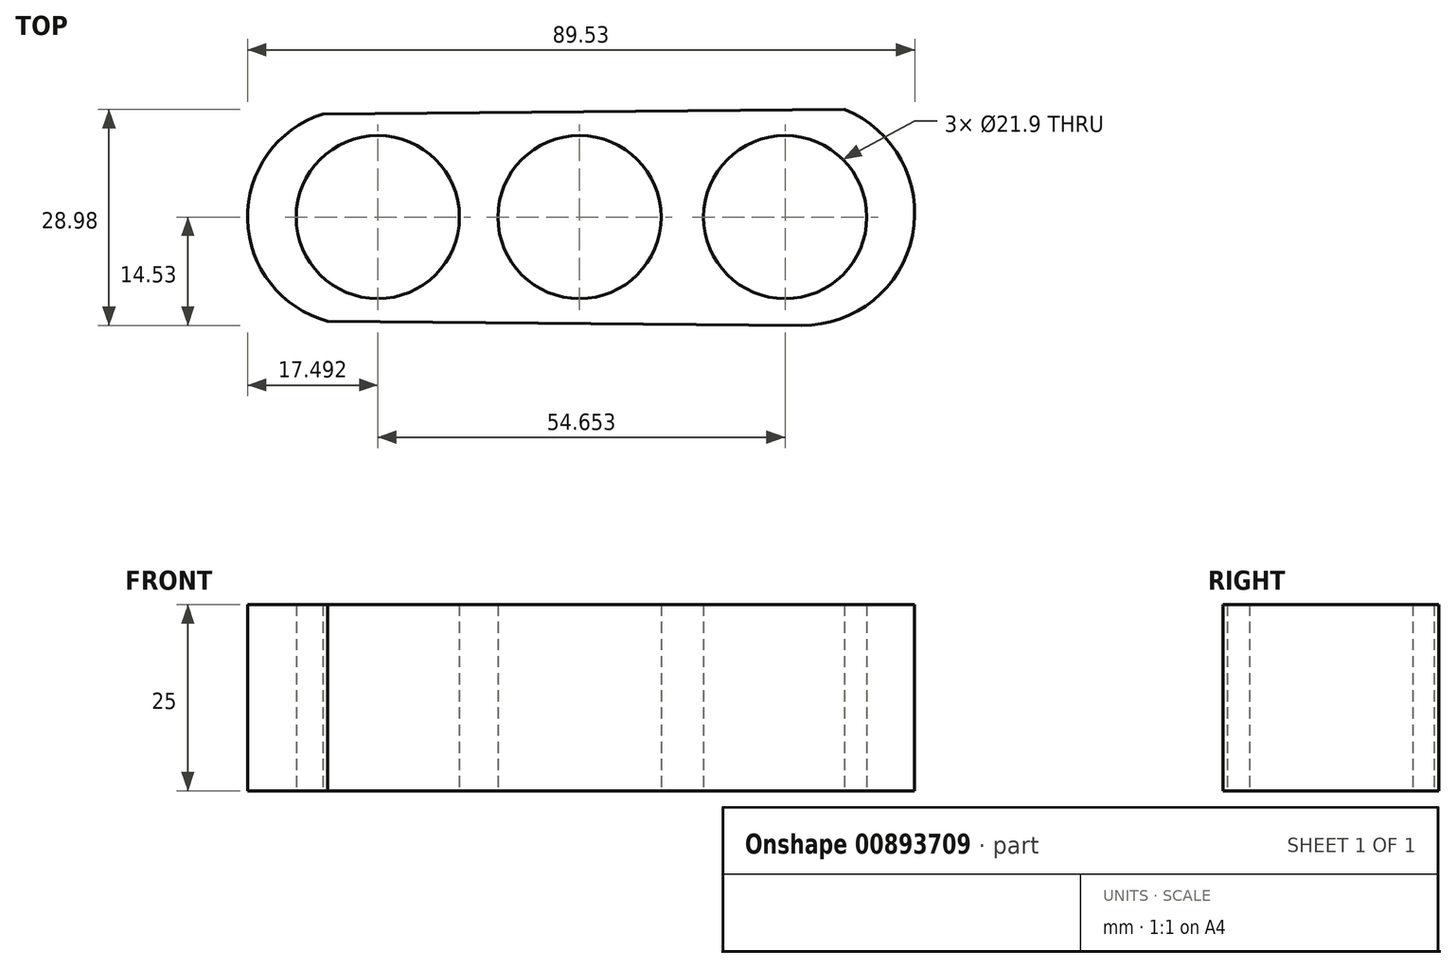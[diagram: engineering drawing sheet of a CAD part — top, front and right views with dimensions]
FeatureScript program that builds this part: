
annotation { "Feature Type Name" : "Feature", "Feature Type Description" : "" }
export const myFeature = defineFeature(function(context is Context, id is Id, definition is map)
    precondition{}
    {
        {
            var Q0;
            Q0=qCreatedBy(makeId("Top.planeOp"),FACE);
            var sketch = newSketch(context, id + "F0", { "sketchPlane" : qUnion([Q0])});
            skCircle(sketch, "E0", {"center": v(0, 0) * mm, "radius": 10.95 * mm});
            skCircle(sketch, "E1", {"center": v(-27.07, 0) * mm, "radius": 10.95 * mm});
            skCircle(sketch, "E2", {"center": v(27.59, 0) * mm, "radius": 10.95 * mm});
            skArc(sketch, "E3", {"start": v(-34.43, 13.82) * mm, "mid": v(-44.55, -0.3) * mm, "end": v(-33.79, -13.95) * mm});
            skLineSegment(sketch, "E4", {"start": v(-33.79, -13.95) * mm, "end": v(29.8, -14.53) * mm});
            skArc(sketch, "E5", {"start": v(29.8, -14.53) * mm, "mid": v(44.68, -2.43) * mm, "end": v(35.56, 14.45) * mm});
            skPoint(sketch, "E6.end.orphan", {"position": v(0, 15.5) * mm});
            skLineSegment(sketch, "E7", {"start": v(-34.43, 13.82) * mm, "end": v(35.56, 14.45) * mm});
            skSolve(sketch);
        }
        {
            var Q0;
            Q0=makeQuery(id+"F0.imprint","IMPRINT",FACE,{"disambiguationData":[TD([[makeQuery(id+"F0.imprint","IMPRINT",EDGE,{"derivedFrom":sQuery(id+"F0.wireOp",EDGE,"E0")}),-1.0]])]});
            extrude(context, id + "F1", {"entities" : qUnion([Q0]), "depth" : 25 * mm, "offsetDistance" : 25 * mm});
        }
    });
